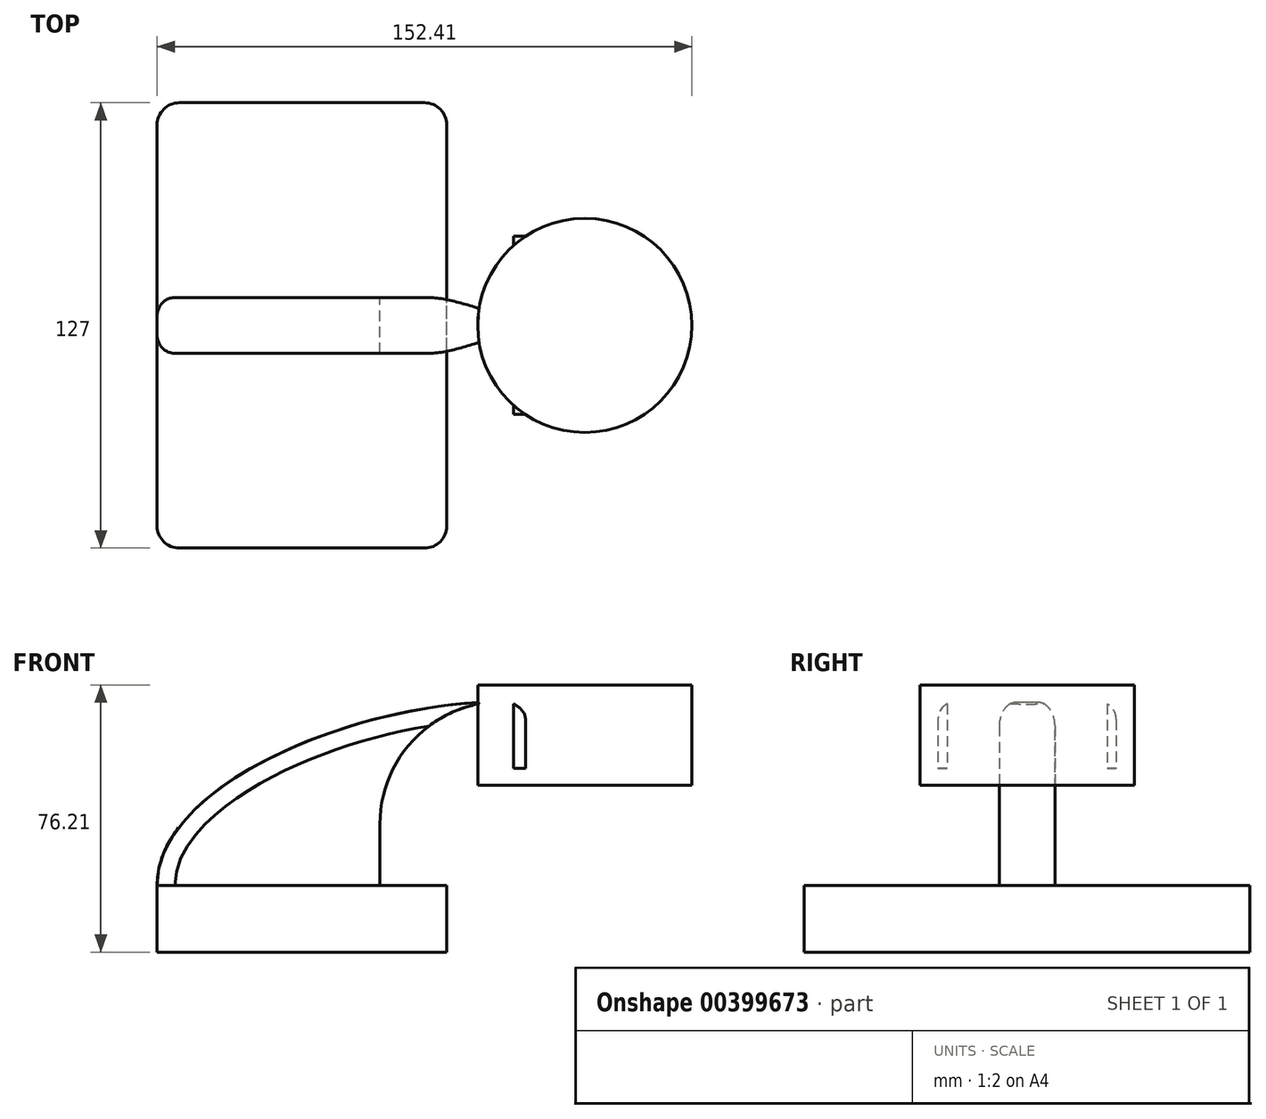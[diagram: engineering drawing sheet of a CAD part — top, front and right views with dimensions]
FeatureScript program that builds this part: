
annotation { "Feature Type Name" : "Feature", "Feature Type Description" : "" }
export const myFeature = defineFeature(function(context is Context, id is Id, definition is map)
    precondition{}
    {
        {
            var Q0;
            Q0=qCreatedBy(makeId("Front.planeOp"),FACE);
            var sketch = newSketch(context, id + "F0", { "sketchPlane" : qUnion([Q0])});
            skLineSegment(sketch, "E0.bottom", {"start": v(-41.28, 9.53) * mm, "end": v(41.27, 9.53) * mm});
            skLineSegment(sketch, "E0.top", {"start": v(-41.28, -9.52) * mm, "end": v(41.28, -9.52) * mm});
            skLineSegment(sketch, "E0.left", {"start": v(-41.28, 9.53) * mm, "end": v(-41.28, -9.52) * mm});
            skLineSegment(sketch, "E0.right", {"start": v(41.27, 9.53) * mm, "end": v(41.27, -9.52) * mm});
            skPoint(sketch, "E0.middle", {"position": v(0, 0) * mm});
            skLineSegment(sketch, "E1.bottom", {"start": v(111.12, 38.1) * mm, "end": v(60.32, 38.1) * mm});
            skLineSegment(sketch, "E1.top", {"start": v(111.12, 66.68) * mm, "end": v(60.32, 66.68) * mm});
            skLineSegment(sketch, "E1.left", {"start": v(111.12, 38.1) * mm, "end": v(111.12, 66.68) * mm});
            skLineSegment(sketch, "E1.right", {"start": v(60.32, 38.1) * mm, "end": v(60.32, 66.68) * mm});
            skPoint(sketch, "E1.middle", {"position": v(85.72, 52.39) * mm});
            skLineSegment(sketch, "E2.bottom", {"start": v(41.28, 27) * mm, "end": v(41.28, 27) * mm});
            skArc(sketch, "E3", {"start": v(41.28, 27) * mm, "mid": v(45.92, 38.23) * mm, "end": v(57.15, 42.88) * mm});
            skLineSegment(sketch, "E4", {"start": v(57.15, 42.88) * mm, "end": v(80.6, 42.88) * mm});
            skPoint(sketch, "E5", {"position": v(41.27, 9.53) * mm});
            skLineSegment(sketch, "E6", {"start": v(41.28, 27) * mm, "end": v(41.27, 9.53) * mm});
            skLineSegment(sketch, "E7.0", {"start": v(22.22, 27) * mm, "end": v(22.22, 9.53) * mm});
            skArc(sketch, "E7.1", {"start": v(22.22, 27) * mm, "mid": v(32.45, 51.7) * mm, "end": v(57.15, 61.93) * mm});
            skLineSegment(sketch, "E7.2", {"start": v(57.15, 61.93) * mm, "end": v(80.6, 61.93) * mm});
            skLineSegment(sketch, "E8", {"start": v(80.6, 38.1) * mm, "end": v(80.6, 66.68) * mm});
            skFitSpline(sketch, "E9", {"points": [v(-41.28, 9.52) * mm, v(57.15, 61.93) * mm], "startDerivative": vector(-0.63, 85.14) * mm, "endDerivative": vector(128.8, 0.96) * mm});
            skSolve(sketch);
        }
        {
            var Q0;
            Q0=makeQuery(id+"F0.imprint","IMPRINT",FACE,{"disambiguationData":[TD([[makeQuery(id+"F0.imprint","IMPRINT",EDGE,{"derivedFrom":sQuery(id+"F0.wireOp",EDGE,"E0.top")}),1.0]])]});
            extrude(context, id + "F1", {"entities" : qUnion([Q0]), "endBound" : BoundingType.SYMMETRIC, "depth" : 127 * mm});
        }
        {
            var Q0;
            {var subQ1=sQuery(id+"F0.wireOp",EDGE,"E3");Q0=makeQuery(id+"F0.imprint","IMPRINT",FACE,{"disambiguationData":[TD([[makeQuery(id+"F0.imprint","IMPRINT",EDGE,{"derivedFrom":subQ1}),1.0]])]});}
            var Q1;
            {var subQ0=sQuery(id+"F0.wireOp",EDGE,"E4");var subQ1=sQuery(id+"F0.wireOp",EDGE,"E1.right");var subQ2=makeQuery(id+"F0.imprint","INTERSECT",VERTEX,{"derivedFrom":[subQ1,subQ0]});Q1=makeQuery(id+"F0.imprint","IMPRINT",FACE,{"disambiguationData":[TD([[makeQuery(id+"F0.imprint","IMPRINT",EDGE,{"disambiguationData":[TD([[subQ2,-1.0]])],"derivedFrom":subQ1}),-1.0]])]});}
            extrude(context, id + "F2", {"entities" : qUnion([Q0, Q1]), "operationType" : NewBodyOperationType.ADD, "endBound" : BoundingType.SYMMETRIC, "depth" : 50.8 * mm});
        }
        {
            var Q0;
            {var subQ3=sQuery(id+"F0.wireOp",EDGE,"E7.0");Q0=makeQuery(id+"F0.imprint","IMPRINT",FACE,{"disambiguationData":[TD([[makeQuery(id+"F0.imprint","IMPRINT",EDGE,{"derivedFrom":subQ3}),-1.0]])]});}
            extrude(context, id + "F3", {"entities" : qUnion([Q0]), "operationType" : NewBodyOperationType.ADD, "endBound" : BoundingType.SYMMETRIC, "depth" : 15.88 * mm});
        }
        {
            var Q0;
            {var subQ0=sQuery(id+"F0.wireOp",EDGE,"E1.left");Q0=makeQuery(id+"F0.imprint","IMPRINT",FACE,{"disambiguationData":[TD([[makeQuery(id+"F0.imprint","IMPRINT",EDGE,{"derivedFrom":subQ0}),1.0]])]});}
            var Q1;
            Q1=sQuery(id+"F0.wireOp",EDGE,"E8");
            revolve(context, id + "F4", {"operationType" : NewBodyOperationType.ADD, "entities" : qUnion([Q0]), "axis" : qUnion([Q1]), "revolveType" : RevolveType.FULL});
        }
        {
            var Q0;
            Q0=makeQuery(id+"F1.opExtrude","CAP_EDGE",EDGE,{"disambiguationData":[OSD([sQuery(id+"F0.wireOp",EDGE,"E0.right")])],"isStart":false});
            var Q1;
            Q1=makeQuery(id+"F1.opExtrude","CAP_EDGE",EDGE,{"disambiguationData":[OSD([sQuery(id+"F0.wireOp",EDGE,"E0.left")])],"isStart":false});
            var Q2;
            Q2=makeQuery(id+"F1.opExtrude","CAP_EDGE",EDGE,{"disambiguationData":[OSD([sQuery(id+"F0.wireOp",EDGE,"E0.right")])],"isStart":true});
            var Q3;
            Q3=makeQuery(id+"F1.opExtrude","CAP_EDGE",EDGE,{"disambiguationData":[OSD([sQuery(id+"F0.wireOp",EDGE,"E0.left")])],"isStart":true});
            fillet(context, id + "F5", {"entities" : qUnion([Q0, Q1, Q2, Q3]), "radius" : 6.35 * mm, "tangentPropagation" : true, "allowEdgeOverflow" : false});
        }
        {
            var Q0;
            Q0=makeQuery(id+"F2.opExtrude","CAP_EDGE",EDGE,{"disambiguationData":[OSD([sQuery(id+"F0.wireOp",EDGE,"E7.1")])],"isStart":true});
            var Q1;
            Q1=makeQuery(id+"F2.opExtrude","CAP_EDGE",EDGE,{"disambiguationData":[OSD([sQuery(id+"F0.wireOp",EDGE,"E7.0")])],"isStart":true});
            var Q2;
            Q2=makeQuery(id+"F2.opExtrude","CAP_EDGE",EDGE,{"disambiguationData":[OSD([sQuery(id+"F0.wireOp",EDGE,"E7.2")])],"isStart":true});
            var Q3;
            Q3=makeQuery(id+"F2.opExtrude","CAP_EDGE",EDGE,{"disambiguationData":[OSD([sQuery(id+"F0.wireOp",EDGE,"E7.2")])],"isStart":false});
            var Q4;
            Q4=makeQuery(id+"F2.opExtrude","CAP_EDGE",EDGE,{"disambiguationData":[OSD([sQuery(id+"F0.wireOp",EDGE,"E7.1")])],"isStart":false});
            var Q5;
            Q5=makeQuery(id+"F2.opExtrude","CAP_EDGE",EDGE,{"disambiguationData":[OSD([sQuery(id+"F0.wireOp",EDGE,"E7.0")])],"isStart":false});
            var Q6;
            Q6=makeQuery(id+"F3.opExtrude","CAP_EDGE",EDGE,{"disambiguationData":[OSD([sQuery(id+"F0.wireOp",EDGE,"E9")])],"isStart":true});
            var Q7;
            Q7=makeQuery(id+"F3.opExtrude","CAP_EDGE",EDGE,{"disambiguationData":[OSD([sQuery(id+"F0.wireOp",EDGE,"E9")])],"isStart":false});
            fillet(context, id + "F6", {"entities" : qUnion([Q0, Q1, Q2, Q3, Q4, Q5, Q6, Q7]), "radius" : 5.08 * mm, "tangentPropagation" : true, "allowEdgeOverflow" : false});
        }
    });
